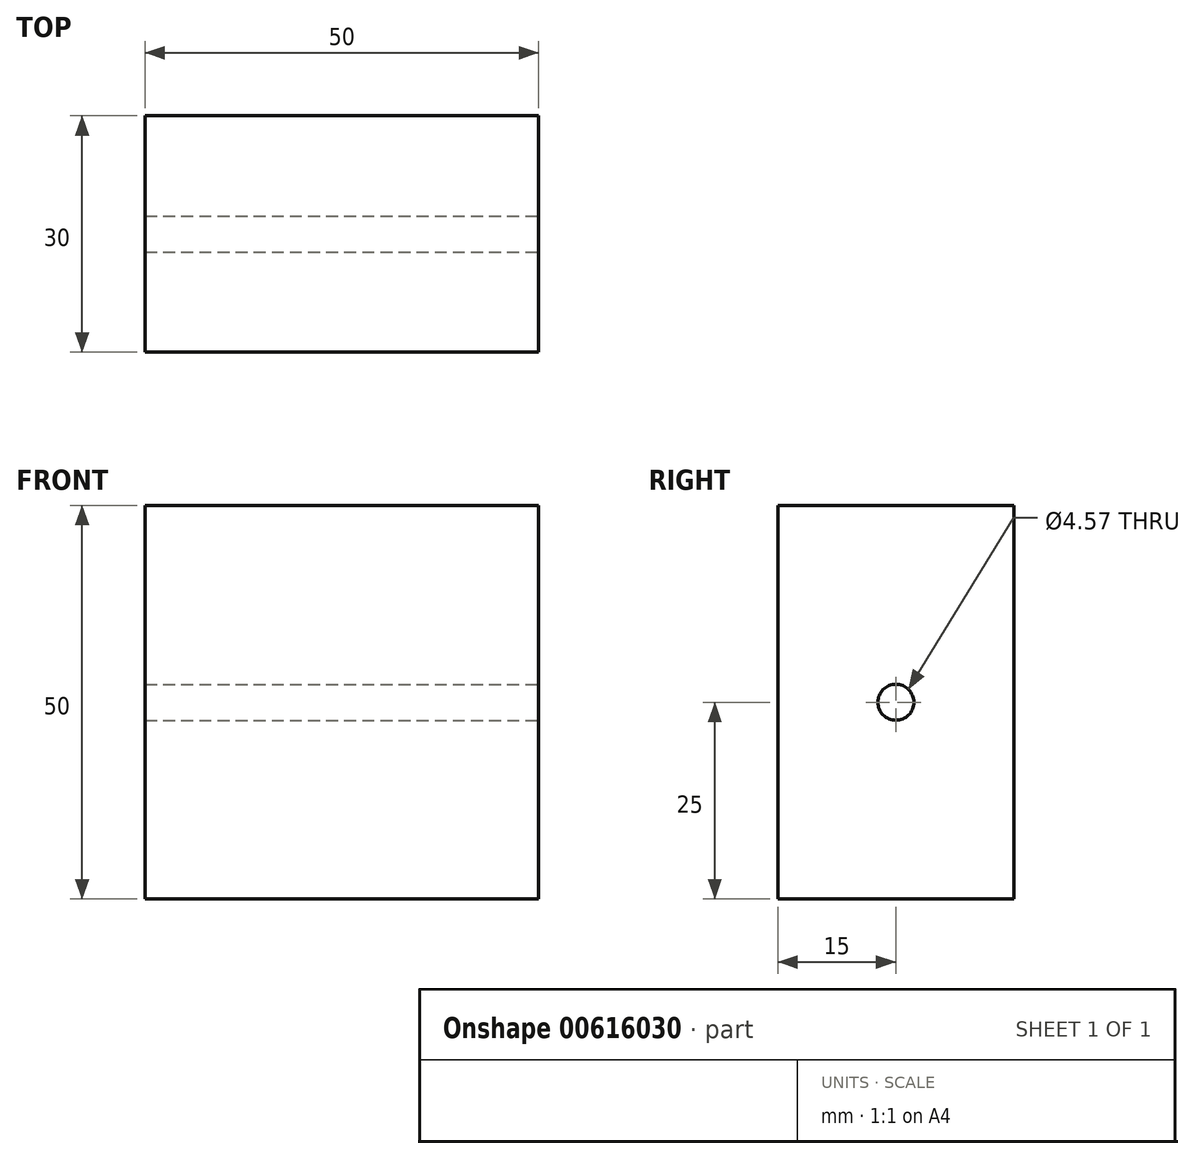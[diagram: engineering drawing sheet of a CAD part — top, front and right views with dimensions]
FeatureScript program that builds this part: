
annotation { "Feature Type Name" : "Feature", "Feature Type Description" : "" }
export const myFeature = defineFeature(function(context is Context, id is Id, definition is map)
    precondition{}
    {
        {
            var Q0;
            Q0=qCreatedBy(makeId("Front.planeOp"),FACE);
            var sketch = newSketch(context, id + "F0", { "sketchPlane" : qUnion([Q0])});
            skLineSegment(sketch, "E0.bottom", {"start": v(25, 25) * mm, "end": v(-25, 25) * mm});
            skLineSegment(sketch, "E0.top", {"start": v(25, -25) * mm, "end": v(-25, -25) * mm});
            skLineSegment(sketch, "E0.left", {"start": v(25, 25) * mm, "end": v(25, -25) * mm});
            skLineSegment(sketch, "E0.right", {"start": v(-25, 25) * mm, "end": v(-25, -25) * mm});
            skPoint(sketch, "E0.middle", {"position": v(0, 0) * mm});
            skSolve(sketch);
        }
        {
            var Q0;
            Q0 = qSketchRegion(id + "F0", true);
            extrude(context, id + "F1", {"entities" : qUnion([Q0]), "depth" : 30 * mm, "offsetDistance" : 25 * mm});
        }
        {
            var Q0;
            Q0=makeQuery(id+"F1.opExtrude","SWEPT_FACE",FACE,{"disambiguationData":[OSD([sQuery(id+"F0.wireOp",EDGE,"E0.left")])]});
            var sketch = newSketch(context, id + "F2", { "sketchPlane" : qUnion([Q0])});
            skLineSegment(sketch, "E1", {"start": v(-30, 25) * mm, "end": v(0, -25) * mm, "construction": true});
            skLineSegment(sketch, "E2", {"start": v(0, 25) * mm, "end": v(-30, -25) * mm, "construction": true});
            skCircle(sketch, "E3", {"center": v(-15, 0) * mm, "radius": 2.29 * mm});
            skSolve(sketch);
        }
        {
            var Q0;
            Q0 = qSketchRegion(id + "F2", true);
            extrude(context, id + "F3", {"entities" : qUnion([Q0]), "operationType" : NewBodyOperationType.REMOVE, "endBound" : BoundingType.THROUGH_ALL, "oppositeDirection" : true, "depth" : 25 * mm, "offsetDistance" : 25 * mm});
        }
    });
